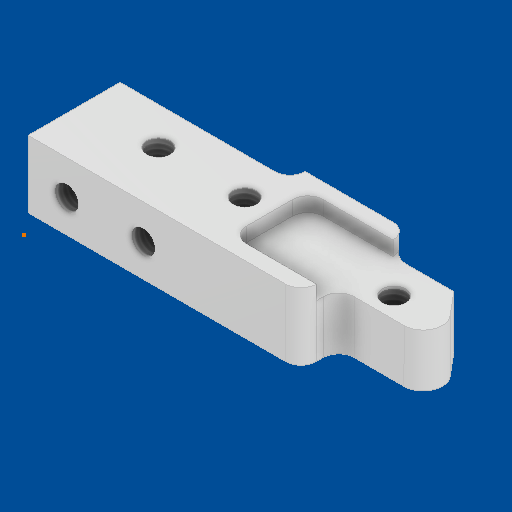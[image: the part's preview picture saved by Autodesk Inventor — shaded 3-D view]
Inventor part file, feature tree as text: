
AUTODESK INVENTOR PART (.ipt)
format: ipt  version: 2025 (Build 290162000, 162)  size: 361,984 bytes
history: native  units: in
note: dims shown in document units (in); Inventor stores cm internally (conversion verified against a paired STEP export)
features: move_body x20, direct_edit x19, sketch x6, other x6, hole x4, fillet x2, plane x1, split x1
ambient origin geometry x8: Origin, YZ Plane, XZ Plane, XY Plane, X Axis, Y Axis, Z Axis, Center Point
bodies: Solid1 (feature_tree), Body8 (feature_tree)
feature tree (59):
  direct_edit  "Direct Edit1"
  move_body  "Move Body1"
  move_body  "Move Body2"
  move_body  "Move Body3"
  move_body  "Move Body4"
  fillet  "Fillet1"  Radius=0.0962in
  sketch  "Sketch1"  dims[d0=0.0in d1=0.0in d2=0.375in d3=0.0962in]
  sketch  "Sketch2"  dims[d4=45.0deg d5=-0.875in d6=-0.375in d7=1.25in]
  plane  "Work Plane1"
  split  "Split1"
  direct_edit  "Direct Edit2"
  direct_edit  "Direct Edit3"
  direct_edit  "Direct Edit4"
  direct_edit  "Direct Edit5"
  hole  "Hole1"  [1 undecoded]
  hole  "Hole2"  [1 undecoded]
  hole  "Hole3"  [1 undecoded]
  direct_edit  "Direct Edit6"
  hole  "Hole4"  [1 undecoded]
  direct_edit  "Direct Edit7"
  fillet  "Fillet2"  Radius=0.0394in
  direct_edit  "Direct Edit8"
  direct_edit  "Direct Edit9"
  direct_edit  "Direct Edit10"
  direct_edit  "Direct Edit11"
  direct_edit  "Direct Edit12"
  direct_edit  "Direct Edit13"
  direct_edit  "Direct Edit14"
  direct_edit  "Direct Edit15"
  direct_edit  "Direct Edit16"
  direct_edit  "Direct Edit17"
  direct_edit  "Direct Edit18"
  direct_edit  "Direct Edit19"
  sketch  "Sketch3"  dims[d8=0.3937in d9=0.0in d10=0.0in d11=0.0787in d12=0.4724in]
  sketch  "Sketch4"  dims[d13=0.0in d14=0.0in d15=0.0787in d16=0.0in d17=0.0in d18=-0.006in]
  sketch  "Sketch5"  dims[d19=0.0394in d20=0.0394in d21=0.0394in]
  sketch  "Sketch6"  dims[d22=0.0968in d23=2.3622in d24=0.1575in d25=0.0787in d26=90.0deg d27=3.1811in d28=0.8108in d29=0.0968in d30=2.3622in d31=0.1575in d32=0.0787in d33=90.0deg d34=3.1811in d35=0.8108in d36=0.0968in d37=0.7874in d38=0.1575in d39=0.0787in d40=90.0deg d41=3.5433in d42=0.0in d43=0.0394in d44=0.0968in d45=2.3622in d46=0.1575in d47=0.0787in d48=90.0deg d49=3.1811in d50=0.8108in d51=0.0in d52=0.0in d53=-0.0008in d54=0.063in d69=0.0in d70=0.0in d71=-0.0295in d72=0.0in d73=0.0in d74=-0.0154in d75=-0.0098in d76=0.0197in d77=0.0in d78=0.0055in d79=0.0in d80=0.0114in d81=0.0in d82=0.0in d83=0.0in d84=0.0in d85=0.0114in d86=-0.0114in d87=0.0in d88=0.0in d89=0.0in d90=0.0039in d91=0.0in d92=0.0043in d93=0.0in d94=0.0in d95=-0.0126in d96=0.0in d97=0.0in d98=-0.0224in d99=0.0in d100=0.0in d101=0.0004in d102=0.0in d103=0.0in d104=-0.0008in d105=0.0in d106=0.0in]
  move_body  "Move1"
  move_body  "Move2"
  move_body  "Move3"
  other  "Size1"
  other  "Size2"
  other  "Size3"
  other  "Size4"
  move_body  "Move4"
  move_body  "Move5"
  move_body  "Move6"
  other  "Size5"
  other  "Size6"
  move_body  "Move7"
  move_body  "Move8"
  move_body  "Move9"
  move_body  "Move10"
  move_body  "Move11"
  move_body  "Move12"
  move_body  "Move13"
  move_body  "Move14"
  move_body  "Move15"
  move_body  "Move16"
note: 4 required parameter values undecoded (feature->parameter linkage not recoverable at this tier; creation-order binding heuristic only, values carry confidence <= 0.55)
